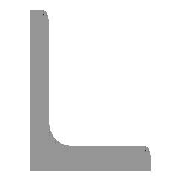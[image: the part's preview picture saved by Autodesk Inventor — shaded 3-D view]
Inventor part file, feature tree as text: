
AUTODESK INVENTOR PART (.ipt)
format: ipt  version: 2016 (Build 200138000, 138)  size: 127,488 bytes
history: native  units: mm (DEFAULTED — no unit token found)
features: other x4, sketch x3, extrude x2, plane x2
ambient origin geometry x8: Origin, YZ Plane, XZ Plane, XY Plane, X Axis, Y Axis, Z Axis, Center Point
bodies: Solid1 (feature_tree)
feature tree (11):
  parser-record x1  (decoder bookkeeping rows leaked as tree rows — omitted from the tree; the rows remain in map.json)
  other  "Driven Length"
  other  "Plano inicial"
  other  "Plano final"
  extrude  "Cuerpo"  Depth=38.1mm
  sketch  "Boceto5"  dims[d4=2400.0mm d5=0.0mm d10=0.0mm d11=0.0mm d12=-0.0mm d13=2400.0mm d14=4.826mm d15=2.286mm d16=90.0deg d17=2400.0mm d18=10.0mm d19=0.0mm]
  plane  "Plano de trabajo4"
  extrude  "Extrusión2"  Depth=4.7625mm
  sketch  "Sketch3"  dims[d0=38.1mm d1=38.1mm]
  plane  "Work Plane3"
  sketch  "Sketch4"  dims[d2=4.7625mm d3=4.7625mm]
